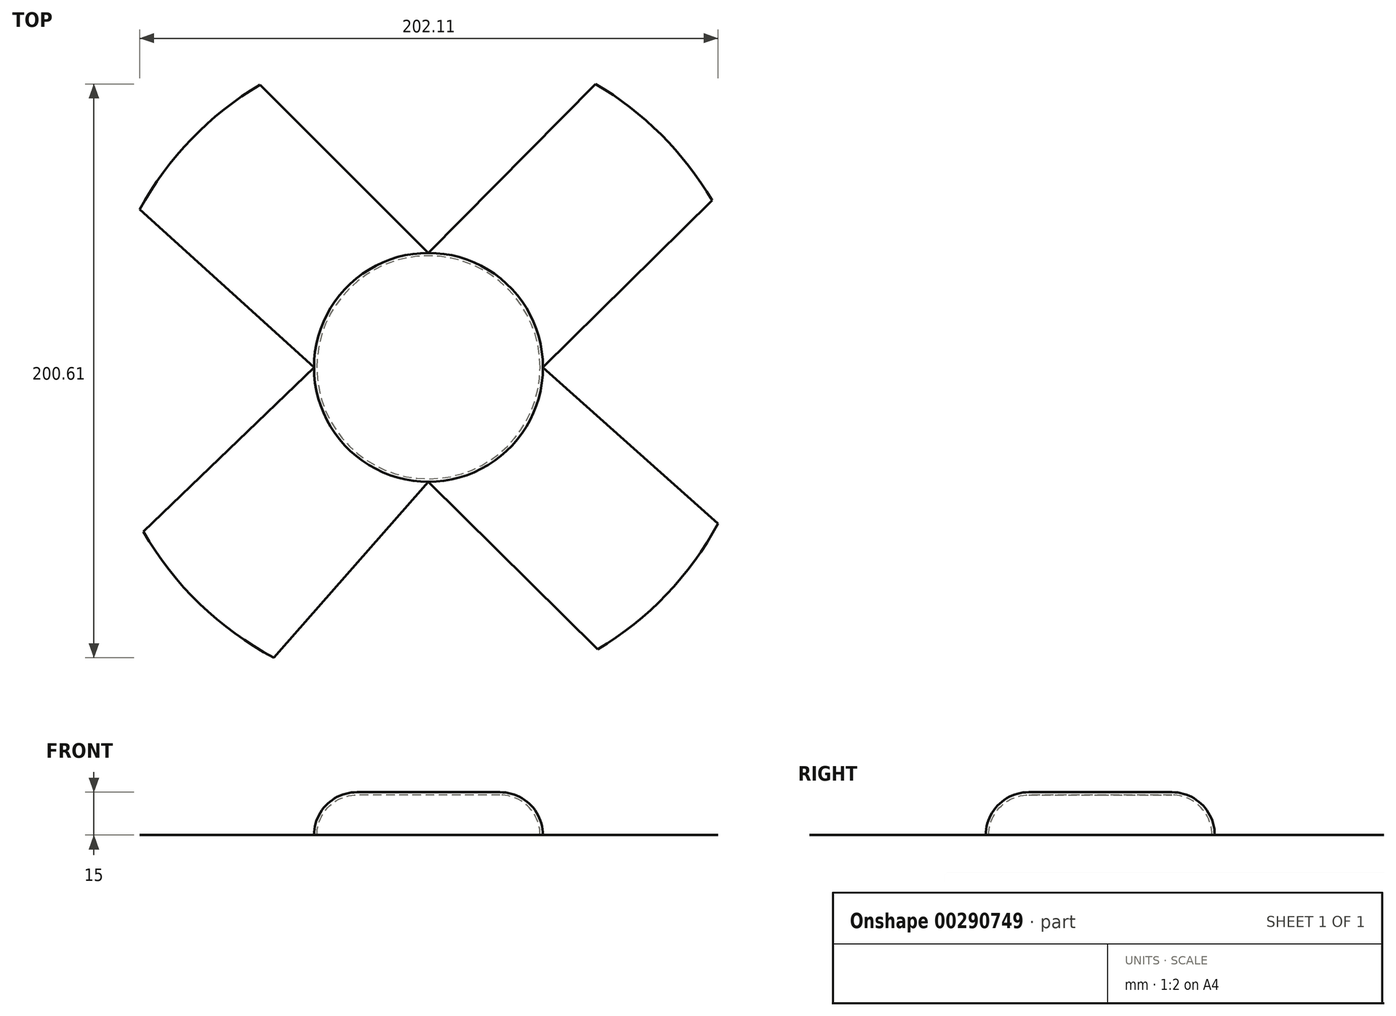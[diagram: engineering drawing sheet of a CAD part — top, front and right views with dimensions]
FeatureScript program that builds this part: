
annotation { "Feature Type Name" : "Feature", "Feature Type Description" : "" }
export const myFeature = defineFeature(function(context is Context, id is Id, definition is map)
    precondition{}
    {
        {
            var Q0;
            Q0=qCreatedBy(makeId("Top.planeOp"),FACE);
            var sketch = newSketch(context, id + "F0", { "sketchPlane" : qUnion([Q0])});
            skCircle(sketch, "E0", {"center": v(0, 0) * mm, "radius": 40 * mm});
            skCircle(sketch, "E1", {"center": v(0, 0) * mm, "radius": 115 * mm});
            skLineSegment(sketch, "E2", {"start": v(-40, 0) * mm, "end": v(-99.62, -57.45) * mm});
            skLineSegment(sketch, "E3", {"start": v(-40, 0) * mm, "end": v(-100.9, 55.17) * mm});
            skLineSegment(sketch, "E4", {"start": v(40, 0) * mm, "end": v(101.21, -54.6) * mm});
            skLineSegment(sketch, "E5", {"start": v(40, 0) * mm, "end": v(99.08, 58.37) * mm});
            skLineSegment(sketch, "E6", {"start": v(0, -40) * mm, "end": v(-54, -101.53) * mm});
            skLineSegment(sketch, "E7", {"start": v(0, -40) * mm, "end": v(59.14, -98.63) * mm});
            skLineSegment(sketch, "E8", {"start": v(0, 40) * mm, "end": v(-58.83, 98.81) * mm});
            skLineSegment(sketch, "E9", {"start": v(0, 40) * mm, "end": v(58.38, 99.08) * mm});
            skSolve(sketch);
        }
        {
            var Q0;
            Q0=makeQuery(id+"F0.imprint","IMPRINT",FACE,{"disambiguationData":[TD([[makeQuery(id+"F0.imprint","IMPRINT",EDGE,{"derivedFrom":sQuery(id+"F0.wireOp",EDGE,"E0")}),1.0]])]});
            extrude(context, id + "F1", {"entities" : qUnion([Q0]), "depth" : 15 * mm});
        }
        {
            var Q0;
            Q0=makeQuery(id+"F1.opExtrude","CAP_EDGE",EDGE,{"disambiguationData":[OSD([sQuery(id+"F0.wireOp",EDGE,"E0")])],"isStart":false});
            fillet(context, id + "F2", {"entities" : qUnion([Q0]), "radius" : 15 * mm, "tangentPropagation" : true, "allowEdgeOverflow" : false});
        }
        {
            var Q0;
            Q0=makeQuery(id+"F1.opExtrude","CAP_FACE",FACE,{"disambiguationData":[OSD([sQuery(id+"F0.wireOp",EDGE,"E0")])],"isStart":true});
            shell(context, id + "F3", {"entities" : qUnion([Q0]), "thickness" : 1 * mm});
        }
        {
            var Q0;
            Q0=makeQuery(id+"F0.imprint","IMPRINT",FACE,{"disambiguationData":[TD([[makeQuery(id+"F0.imprint","IMPRINT",EDGE,{"derivedFrom":sQuery(id+"F0.wireOp",EDGE,"E0")}),-1.0]])]});
            extrude(context, id + "F4", {"entities" : qUnion([Q0]), "operationType" : NewBodyOperationType.ADD, "depth" : 0.1 * mm});
        }
    });
